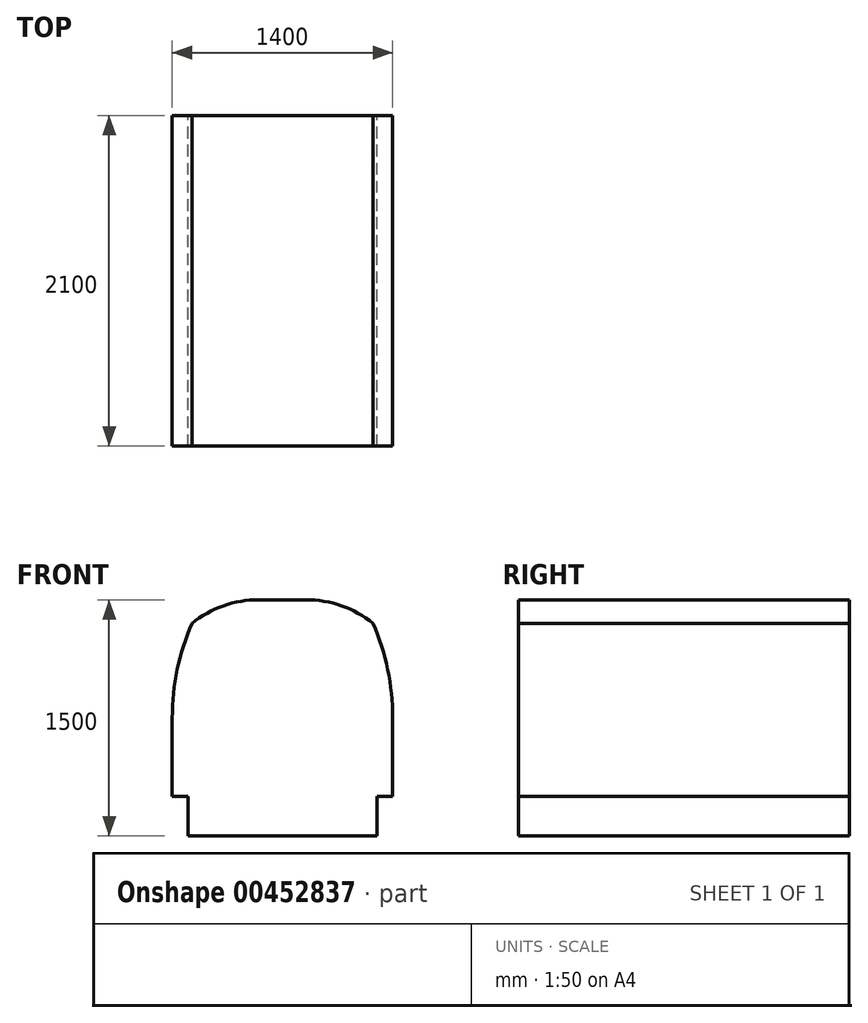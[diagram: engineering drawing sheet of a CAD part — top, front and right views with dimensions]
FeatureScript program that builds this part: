
annotation { "Feature Type Name" : "Feature", "Feature Type Description" : "" }
export const myFeature = defineFeature(function(context is Context, id is Id, definition is map)
    precondition{}
    {
        {
            var Q0;
            Q0=qCreatedBy(makeId("Front.planeOp"),FACE);
            var sketch = newSketch(context, id + "F0", { "sketchPlane" : qUnion([Q0])});
            skLineSegment(sketch, "E0", {"start": v(-600, 0) * mm, "end": v(600, 0) * mm});
            skLineSegment(sketch, "E1", {"start": v(-600, 0) * mm, "end": v(-600, 300) * mm});
            skLineSegment(sketch, "E2", {"start": v(600, 0) * mm, "end": v(600, 300) * mm});
            skLineSegment(sketch, "E3", {"start": v(-600, 300) * mm, "end": v(600, 300) * mm, "construction": true});
            skLineSegment(sketch, "E4", {"start": v(-150, 1500) * mm, "end": v(150, 1500) * mm});
            skLineSegment(sketch, "E5", {"start": v(0, 0) * mm, "end": v(0, 1500) * mm, "construction": true});
            skLineSegment(sketch, "E6", {"start": v(-575, 1350) * mm, "end": v(575, 1350) * mm, "construction": true});
            skPoint(sketch, "E7", {"position": v(0, 1350) * mm});
            skArc(sketch, "E8", {"start": v(-150, 1500) * mm, "mid": v(-375.35, 1461.4) * mm, "end": v(-575, 1350) * mm});
            skArc(sketch, "E9", {"start": v(150, 1500) * mm, "mid": v(375.35, 1461.4) * mm, "end": v(575, 1350) * mm});
            skArc(sketch, "E10", {"start": v(-700, 750) * mm, "mid": v(-668.42, 1056.44) * mm, "end": v(-575, 1350) * mm});
            skPoint(sketch, "E11", {"position": v(-614.36, 1250) * mm});
            skCircle(sketch, "E12", {"center": v(-614.36, 1250) * mm, "radius": 1003.66 * mm, "construction": true});
            skLineSegment(sketch, "E13", {"start": v(-1200, 300) * mm, "end": v(-400, 300) * mm, "construction": true});
            skLineSegment(sketch, "E14", {"start": v(-1200, 300) * mm, "end": v(-1200, 434.91) * mm, "construction": true});
            skLineSegment(sketch, "E15", {"start": v(-700, 750) * mm, "end": v(-700, 250) * mm});
            skArc(sketch, "E16.MirrorCS", {"start": v(700, 750) * mm, "mid": v(668.42, 1056.44) * mm, "end": v(575, 1350) * mm});
            skLineSegment(sketch, "E17.MirrorCS", {"start": v(700, 750) * mm, "end": v(700, 250) * mm});
            skLineSegment(sketch, "E18", {"start": v(-700, 250) * mm, "end": v(-600, 250) * mm});
            skLineSegment(sketch, "E19", {"start": v(700, 250) * mm, "end": v(600, 250) * mm});
            skSolve(sketch);
        }
        {
            var Q0;
            {var subQ0=sQuery(id+"F0.wireOp",EDGE,"E0");Q0=makeQuery(id+"F0.imprint","IMPRINT",FACE,{"disambiguationData":[TD([[makeQuery(id+"F0.imprint","IMPRINT",EDGE,{"derivedFrom":subQ0}),1.0]])]});}
            extrude(context, id + "F1", {"entities" : qUnion([Q0]), "depth" : 2100 * mm});
        }
    });
